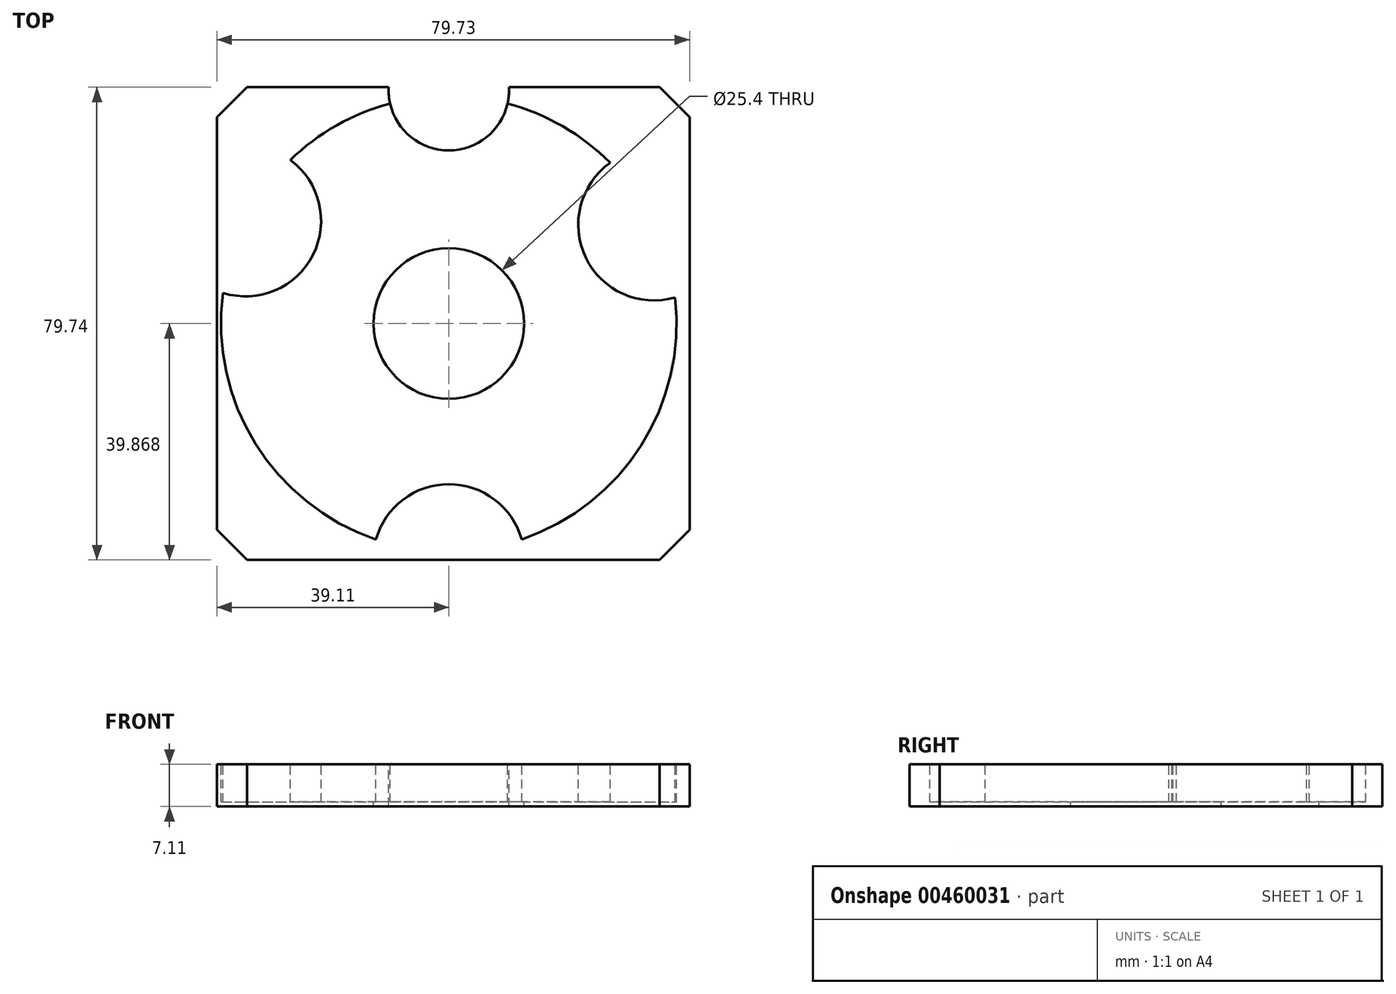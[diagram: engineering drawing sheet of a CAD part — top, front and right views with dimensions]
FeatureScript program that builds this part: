
annotation { "Feature Type Name" : "Feature", "Feature Type Description" : "" }
export const myFeature = defineFeature(function(context is Context, id is Id, definition is map)
    precondition{}
    {
        {
            var Q0;
            Q0=qCreatedBy(makeId("Top.planeOp"),FACE);
            var sketch = newSketch(context, id + "F0", { "sketchPlane" : qUnion([Q0])});
            skLineSegment(sketch, "E0.bottom", {"start": v(40.62, 46.88) * mm, "end": v(-39.11, 46.88) * mm});
            skLineSegment(sketch, "E0.top", {"start": v(40.62, -32.86) * mm, "end": v(-39.11, -32.86) * mm});
            skLineSegment(sketch, "E0.left", {"start": v(40.62, 46.88) * mm, "end": v(40.62, -32.86) * mm});
            skLineSegment(sketch, "E0.right", {"start": v(-39.11, 46.88) * mm, "end": v(-39.11, -32.86) * mm});
            skSolve(sketch);
        }
        {
            var Q0;
            Q0=makeQuery(id+"F0.imprint","IMPRINT",FACE,{"disambiguationData":[TD([[makeQuery(id+"F0.imprint","IMPRINT",EDGE,{"derivedFrom":sQuery(id+"F0.wireOp",EDGE,"E0.bottom")}),1.0]])]});
            extrude(context, id + "F1", {"entities" : qUnion([Q0]), "depth" : 7.11 * mm, "offsetDistance" : 25.4 * mm});
        }
        {
            var Q0;
            Q0=makeQuery(id+"F1.opExtrude","CAP_FACE",FACE,{"disambiguationData":[OSD([sQuery(id+"F0.wireOp",EDGE,"E0.bottom"),sQuery(id+"F0.wireOp",EDGE,"E0.top"),sQuery(id+"F0.wireOp",EDGE,"E0.left"),sQuery(id+"F0.wireOp",EDGE,"E0.right")])],"isStart":false});
            var sketch = newSketch(context, id + "F2", { "sketchPlane" : qUnion([Q0])});
            skCircle(sketch, "E1", {"center": v(0, 7) * mm, "radius": 38.42 * mm});
            skPoint(sketch, "E1.centerSnap0", {"position": v(40.62, 7) * mm});
            skCircle(sketch, "E2", {"center": v(0, -32.86) * mm, "radius": 12.77 * mm});
            skCircle(sketch, "E3", {"center": v(34.61, 23.69) * mm, "radius": 12.78 * mm});
            skCircle(sketch, "E4", {"center": v(-34.29, 24.34) * mm, "radius": 12.74 * mm});
            skSolve(sketch);
        }
        {
            var Q0;
            Q0=makeQuery(id+"F2.imprint","IMPRINT",FACE,{"disambiguationData":[TD([[makeQuery(id+"F2.imprint","IMPRINT",EDGE,{"derivedFrom":sQuery(id+"F2.wireOp",EDGE,"E1")}),1.0]])]});
            extrude(context, id + "F3", {"entities" : qUnion([Q0]), "operationType" : NewBodyOperationType.REMOVE, "oppositeDirection" : true, "depth" : 6.35 * mm, "offsetDistance" : 25.4 * mm});
        }
        {
            var Q0;
            Q0=makeQuery(id+"F1.opExtrude","SWEPT_EDGE",EDGE,{"disambiguationData":[OSD([sQuery(id+"F0.wireOp",EDGE,"E0.bottom"),sQuery(id+"F0.wireOp",EDGE,"E0.left")])]});
            var Q1;
            Q1=makeQuery(id+"F1.opExtrude","SWEPT_EDGE",EDGE,{"disambiguationData":[OSD([sQuery(id+"F0.wireOp",EDGE,"E0.bottom"),sQuery(id+"F0.wireOp",EDGE,"E0.right")])]});
            var Q2;
            Q2=makeQuery(id+"F1.opExtrude","SWEPT_EDGE",EDGE,{"disambiguationData":[OSD([sQuery(id+"F0.wireOp",EDGE,"E0.top"),sQuery(id+"F0.wireOp",EDGE,"E0.left")])]});
            var Q3;
            Q3=makeQuery(id+"F1.opExtrude","SWEPT_EDGE",EDGE,{"disambiguationData":[OSD([sQuery(id+"F0.wireOp",EDGE,"E0.top"),sQuery(id+"F0.wireOp",EDGE,"E0.right")])]});
            chamfer(context, id + "F4", {"entities" : qUnion([Q0, Q1, Q2, Q3]), "width" : 5.08 * mm, "tangentPropagation" : true});
        }
        {
            var Q0;
            Q0=makeQuery(id+"F2.imprint","IMPRINT",FACE,{"disambiguationData":[TD([[makeQuery(id+"F2.imprint","IMPRINT",EDGE,{"derivedFrom":sQuery(id+"F2.wireOp",EDGE,"E1")}),1.0]])]});
            var sketch = newSketch(context, id + "F5", { "sketchPlane" : qUnion([Q0])});
            skCircle(sketch, "E5", {"center": v(0, 7.62) * mm, "radius": 12.95 * mm});
            skSolve(sketch);
        }
        {
            var Q0;
            Q0=sQuery(id+"F2.wireOp",VERTEX,"E1.center");
            var Q1;
            Q1=makeQuery(id+"F1.opExtrude","SWEPT_BODY",BODY,{"disambiguationData":[OSD([sQuery(id+"F0.wireOp",EDGE,"E0.bottom"),sQuery(id+"F0.wireOp",EDGE,"E0.top"),sQuery(id+"F0.wireOp",EDGE,"E0.left"),sQuery(id+"F0.wireOp",EDGE,"E0.right")])]});
            hole(context, id + "F6", {"style" : HoleStyle.SIMPLE, "endStyle" : HoleEndStyle.THROUGH, "holeDiameter" : 25.4 * mm, "majorDiameter" : 6.35 * mm, "isTappedThrough" : true, "tappedDepth" : 12.7 * mm, "tapClearance" : 3, "locations" : qUnion([Q0]), "scope" : qUnion([Q1])});
        }
        {
            var Q0;
            Q0=makeQuery(id+"F2.imprint","IMPRINT",FACE,{"disambiguationData":[TD([[makeQuery(id+"F2.imprint","IMPRINT",EDGE,{"derivedFrom":sQuery(id+"F2.wireOp",EDGE,"E1")}),-1.0]])]});
            var sketch = newSketch(context, id + "F7", { "sketchPlane" : qUnion([Q0])});
            skPoint(sketch, "E6", {"position": v(0, 46.38) * mm});
            skSolve(sketch);
        }
        {
            var Q0;
            Q0=sQuery(id+"F7.wireOp",VERTEX,"E6");
            var Q1;
            Q1=makeQuery(id+"F1.opExtrude","SWEPT_BODY",BODY,{"disambiguationData":[OSD([sQuery(id+"F0.wireOp",EDGE,"E0.bottom"),sQuery(id+"F0.wireOp",EDGE,"E0.top"),sQuery(id+"F0.wireOp",EDGE,"E0.left"),sQuery(id+"F0.wireOp",EDGE,"E0.right")])]});
            hole(context, id + "F8", {"style" : HoleStyle.SIMPLE, "endStyle" : HoleEndStyle.THROUGH, "holeDiameter" : 20.32 * mm, "majorDiameter" : 6.35 * mm, "isTappedThrough" : true, "tappedDepth" : 12.7 * mm, "tapClearance" : 3, "locations" : qUnion([Q0]), "scope" : qUnion([Q1])});
        }
        {
            var Q0;
            Q0=makeQuery(id+"F5.imprint","IMPRINT",FACE,{"disambiguationData":[TD([[makeQuery(id+"F5.imprint","IMPRINT",EDGE,{"derivedFrom":sQuery(id+"F5.wireOp",EDGE,"E5")}),-1.0]])]});
            var Q1;
            Q1 = qSketchRegion(id + "F0", true);
            extrude(context, id + "F9", {"entities" : qUnion([Q0, Q1]), "operationType" : NewBodyOperationType.REMOVE, "oppositeDirection" : true, "depth" : 4.57 * mm, "offsetDistance" : 25.4 * mm});
        }
    });
